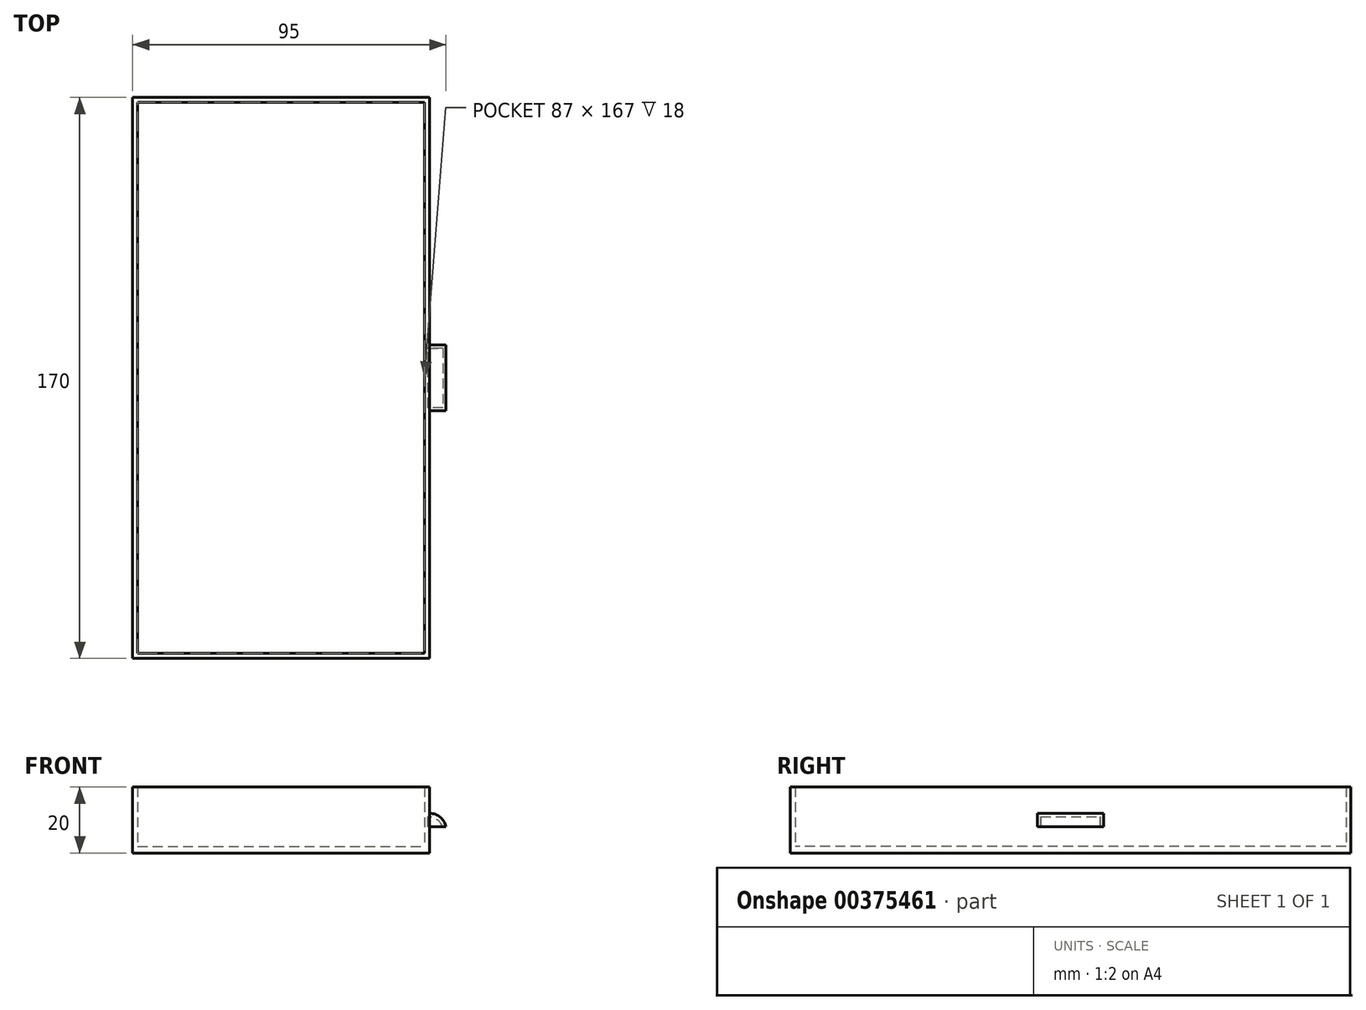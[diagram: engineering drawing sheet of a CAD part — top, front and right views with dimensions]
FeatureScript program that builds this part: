
annotation { "Feature Type Name" : "Feature", "Feature Type Description" : "" }
export const myFeature = defineFeature(function(context is Context, id is Id, definition is map)
    precondition{}
    {
        {
            var Q0;
            Q0=qCreatedBy(makeId("Top.planeOp"),FACE);
            var sketch = newSketch(context, id + "F0", { "sketchPlane" : qUnion([Q0])});
            skLineSegment(sketch, "E0.bottom", {"start": v(-59.07, 120.68) * mm, "end": v(30.93, 120.68) * mm});
            skLineSegment(sketch, "E0.top", {"start": v(-59.07, -49.32) * mm, "end": v(30.93, -49.32) * mm});
            skLineSegment(sketch, "E0.left", {"start": v(-59.07, 120.68) * mm, "end": v(-59.07, -49.32) * mm});
            skLineSegment(sketch, "E0.right", {"start": v(30.93, 120.68) * mm, "end": v(30.93, -49.32) * mm});
            skLineSegment(sketch, "E1.0", {"start": v(-57.57, 119.18) * mm, "end": v(29.43, 119.18) * mm});
            skLineSegment(sketch, "E1.1", {"start": v(-57.57, 119.18) * mm, "end": v(-57.57, -47.82) * mm});
            skLineSegment(sketch, "E1.2", {"start": v(-57.57, -47.82) * mm, "end": v(29.43, -47.82) * mm});
            skLineSegment(sketch, "E1.3", {"start": v(29.43, 119.18) * mm, "end": v(29.43, -47.82) * mm});
            skSolve(sketch);
        }
        {
            var Q0;
            Q0=makeQuery(id+"F0.imprint","IMPRINT",FACE,{"disambiguationData":[TD([[makeQuery(id+"F0.imprint","IMPRINT",EDGE,{"derivedFrom":sQuery(id+"F0.wireOp",EDGE,"E0.bottom")}),-1.0]])]});
            extrude(context, id + "F1", {"entities" : qUnion([Q0]), "depth" : 20 * mm});
        }
        {
            var Q0;
            Q0=makeQuery(id+"F0.imprint","IMPRINT",FACE,{"disambiguationData":[TD([[makeQuery(id+"F0.imprint","IMPRINT",EDGE,{"derivedFrom":sQuery(id+"F0.wireOp",EDGE,"E1.0")}),-1.0]])]});
            extrude(context, id + "F2", {"entities" : qUnion([Q0]), "operationType" : NewBodyOperationType.ADD, "depth" : 2 * mm});
        }
        {
            var Q0;
            Q0=makeQuery(id+"F1.opExtrude","SWEPT_FACE",FACE,{"disambiguationData":[OSD([sQuery(id+"F0.wireOp",EDGE,"E0.right")])]});
            var sketch = newSketch(context, id + "F3", { "sketchPlane" : qUnion([Q0])});
            skLineSegment(sketch, "E2", {"start": v(-49.32, 20) * mm, "end": v(35.68, 20) * mm});
            skPoint(sketch, "E3.endSnap0", {"position": v(-49.32, 10) * mm});
            skLineSegment(sketch, "E4", {"start": v(35.68, 12) * mm, "end": v(45.68, 12) * mm});
            skLineSegment(sketch, "E5", {"start": v(45.68, 12) * mm, "end": v(45.68, 8) * mm});
            skLineSegment(sketch, "E6", {"start": v(45.68, 8) * mm, "end": v(25.68, 8) * mm});
            skLineSegment(sketch, "E7", {"start": v(25.68, 8) * mm, "end": v(25.68, 12) * mm});
            skLineSegment(sketch, "E8", {"start": v(25.68, 12) * mm, "end": v(35.68, 12) * mm});
            skSolve(sketch);
        }
        {
            var Q0;
            Q0=makeQuery(id+"F3.imprint","IMPRINT",FACE,{"disambiguationData":[TD([[makeQuery(id+"F3.imprint","IMPRINT",EDGE,{"derivedFrom":sQuery(id+"F3.wireOp",EDGE,"E4")}),-1.0]])]});
            extrude(context, id + "F4", {"entities" : qUnion([Q0]), "operationType" : NewBodyOperationType.ADD, "depth" : 5 * mm});
        }
        {
            var Q0;
            Q0=makeQuery(id+"F4.opExtrude","SWEPT_FACE",FACE,{"disambiguationData":[OSD([sQuery(id+"F3.wireOp",EDGE,"E6")])]});
            shell(context, id + "F5", {"entities" : qUnion([Q0]), "thickness" : 1 * mm});
        }
        {
            var Q0;
            Q0=makeQuery(id+"F5.opShell","OFFSET_EDGE",EDGE,{"disambiguationData":[OSD([sQuery(id+"F3.wireOp",EDGE,"E4"),sQuery(id+"F3.wireOp",EDGE,"E8")])]});
            var Q1;
            Q1=makeQuery(id+"F4.opExtrude","CAP_EDGE",EDGE,{"disambiguationData":[OSD([sQuery(id+"F3.wireOp",EDGE,"E4"),sQuery(id+"F3.wireOp",EDGE,"E8")])],"isStart":false});
            fillet(context, id + "F6", {"entities" : qUnion([Q0, Q1]), "radius" : 5.08 * mm, "tangentPropagation" : true, "allowEdgeOverflow" : false});
        }
    });
